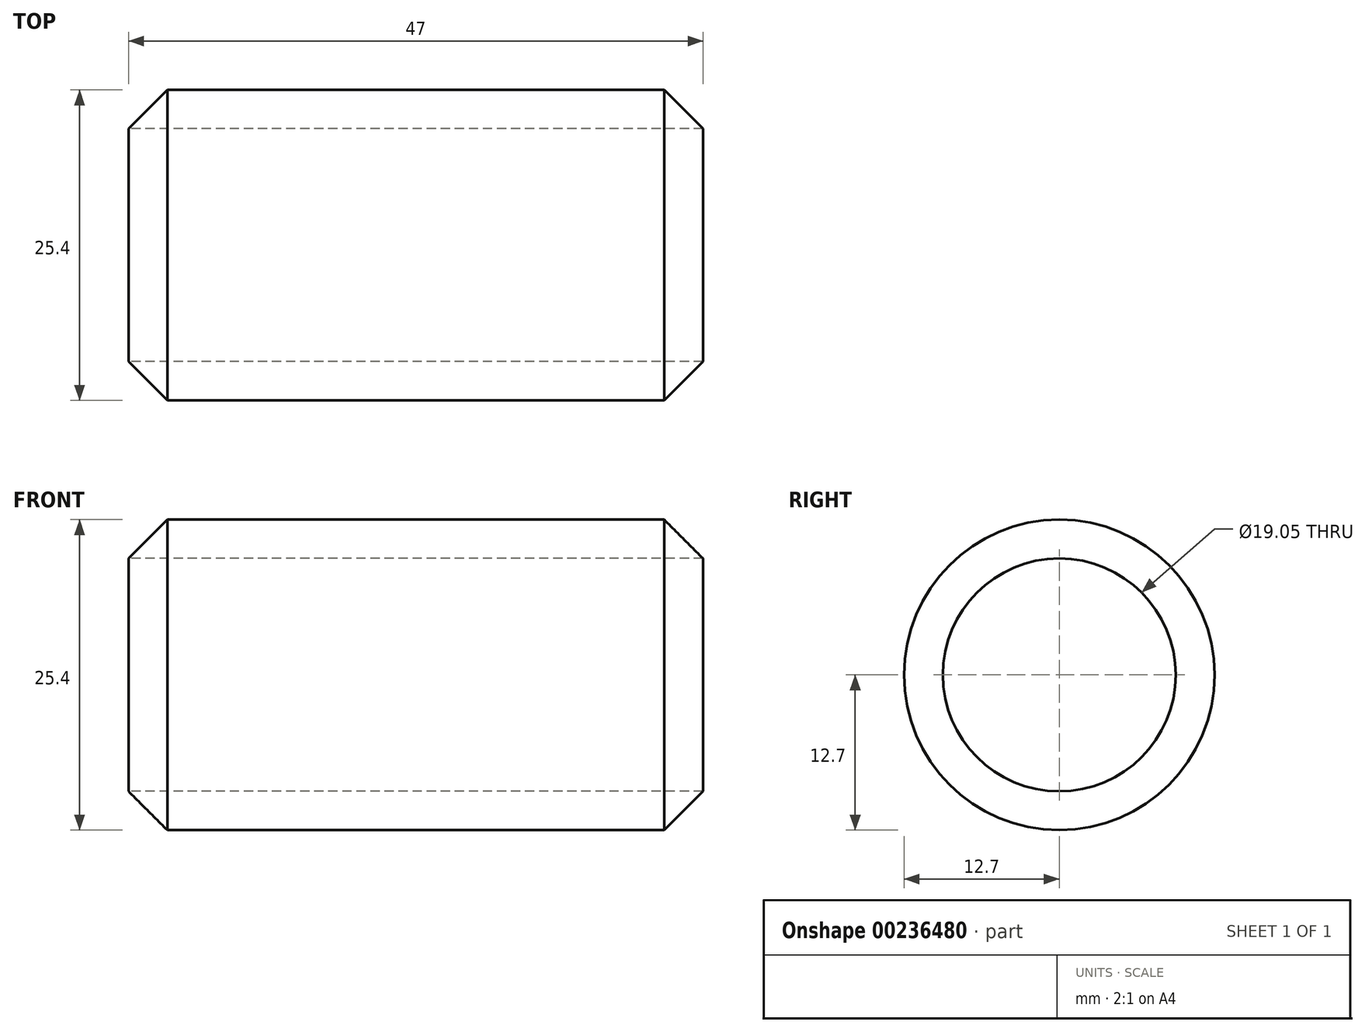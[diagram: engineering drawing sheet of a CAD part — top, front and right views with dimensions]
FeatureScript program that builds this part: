
annotation { "Feature Type Name" : "Feature", "Feature Type Description" : "" }
export const myFeature = defineFeature(function(context is Context, id is Id, definition is map)
    precondition{}
    {
        {
            var Q0;
            Q0=qCreatedBy(makeId("Right.planeOp"),FACE);
            var sketch = newSketch(context, id + "F0", { "sketchPlane" : qUnion([Q0])});
            skCircle(sketch, "E0", {"center": v(0, 0) * mm, "radius": 12.7 * mm});
            skCircle(sketch, "E1", {"center": v(0, 0) * mm, "radius": 9.53 * mm});
            skSolve(sketch);
        }
        {
            var Q0;
            Q0=makeQuery(id+"F0.imprint","IMPRINT",FACE,{"disambiguationData":[TD([[makeQuery(id+"F0.imprint","IMPRINT",EDGE,{"derivedFrom":sQuery(id+"F0.wireOp",EDGE,"E0")}),1.0]])]});
            extrude(context, id + "F1", {"entities" : qUnion([Q0]), "depth" : 50.8 * mm});
        }
        {
            var Q0;
            Q0=makeQuery(id+"F1.opExtrude","CAP_EDGE",EDGE,{"disambiguationData":[OSD([sQuery(id+"F0.wireOp",EDGE,"E0")])],"isStart":false});
            var Q1;
            Q1=makeQuery(id+"F1.opExtrude","SWEPT_FACE",FACE,{"disambiguationData":[OSD([sQuery(id+"F0.wireOp",EDGE,"E0")])]});
            chamfer(context, id + "F2", {"entities" : qUnion([Q0, Q1]), "width" : 5.08 * mm, "tangentPropagation" : true});
        }
    });
